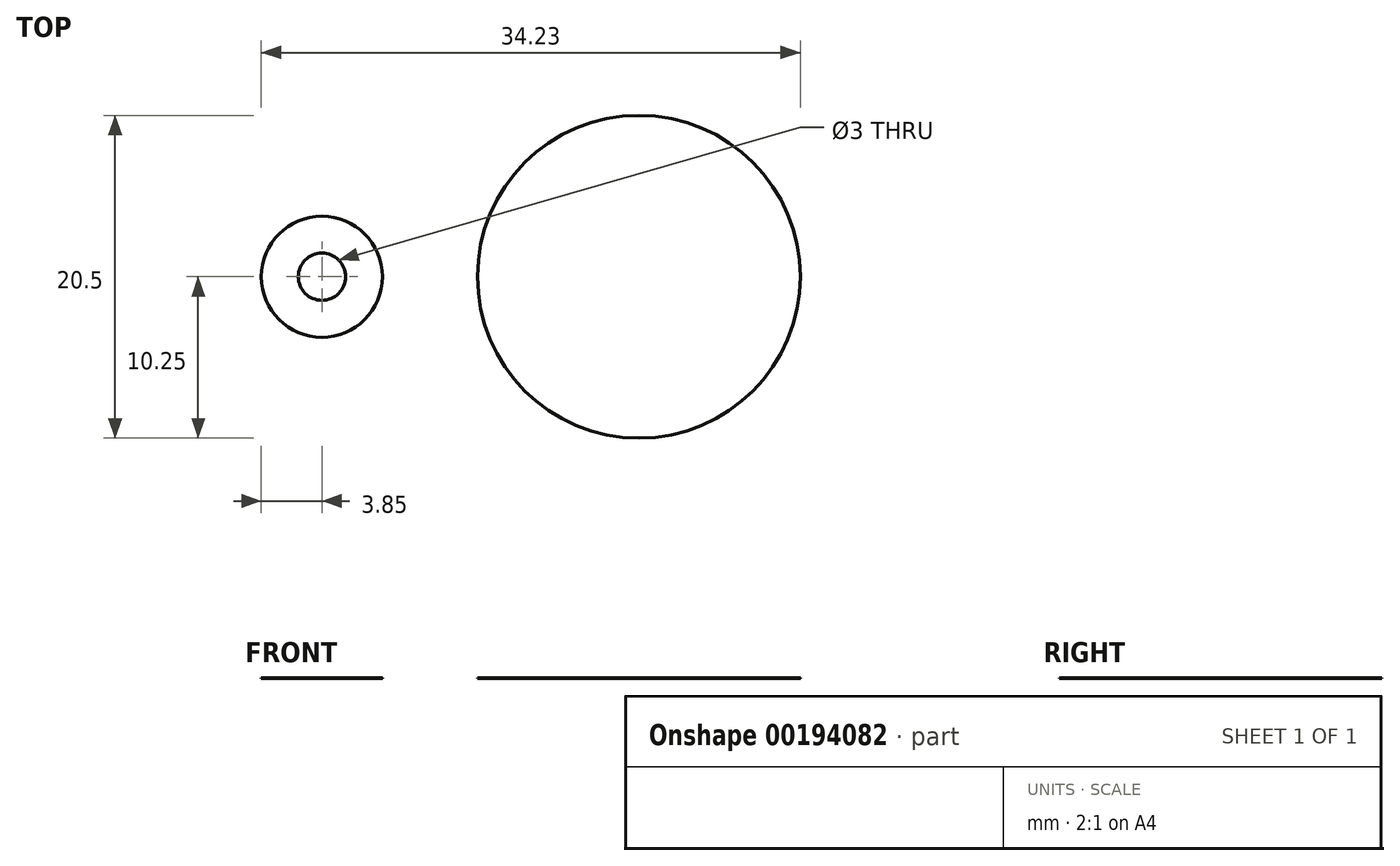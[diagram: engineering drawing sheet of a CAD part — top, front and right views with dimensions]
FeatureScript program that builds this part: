
annotation { "Feature Type Name" : "Feature", "Feature Type Description" : "" }
export const myFeature = defineFeature(function(context is Context, id is Id, definition is map)
    precondition{}
    {
        {
            var Q0;
            Q0=qCreatedBy(makeId("Top.planeOp"),FACE);
            var sketch = newSketch(context, id + "F0", { "sketchPlane" : qUnion([Q0])});
            skCircle(sketch, "E0", {"center": v(0, 0) * mm, "radius": 1.5 * mm});
            skCircle(sketch, "E1", {"center": v(0, 0) * mm, "radius": 3.85 * mm});
            skCircle(sketch, "E2", {"center": v(20.13, 0) * mm, "radius": 10.25 * mm});
            skSolve(sketch);
        }
        {
            var Q0;
            Q0=makeQuery(id+"F0.imprint","IMPRINT",FACE,{"disambiguationData":[TD([[makeQuery(id+"F0.imprint","IMPRINT",EDGE,{"derivedFrom":sQuery(id+"F0.wireOp",EDGE,"E0")}),-1.0]])]});
            var Q1;
            Q1=makeQuery(id+"F0.imprint","IMPRINT",FACE,{"disambiguationData":[TD([[makeQuery(id+"F0.imprint","IMPRINT",EDGE,{"derivedFrom":sQuery(id+"F0.wireOp",EDGE,"E2")}),1.0]])]});
            extrude(context, id + "F1", {"entities" : qUnion([Q0, Q1]), "depth" : 1 / 203.2 * mm});
        }
    });
